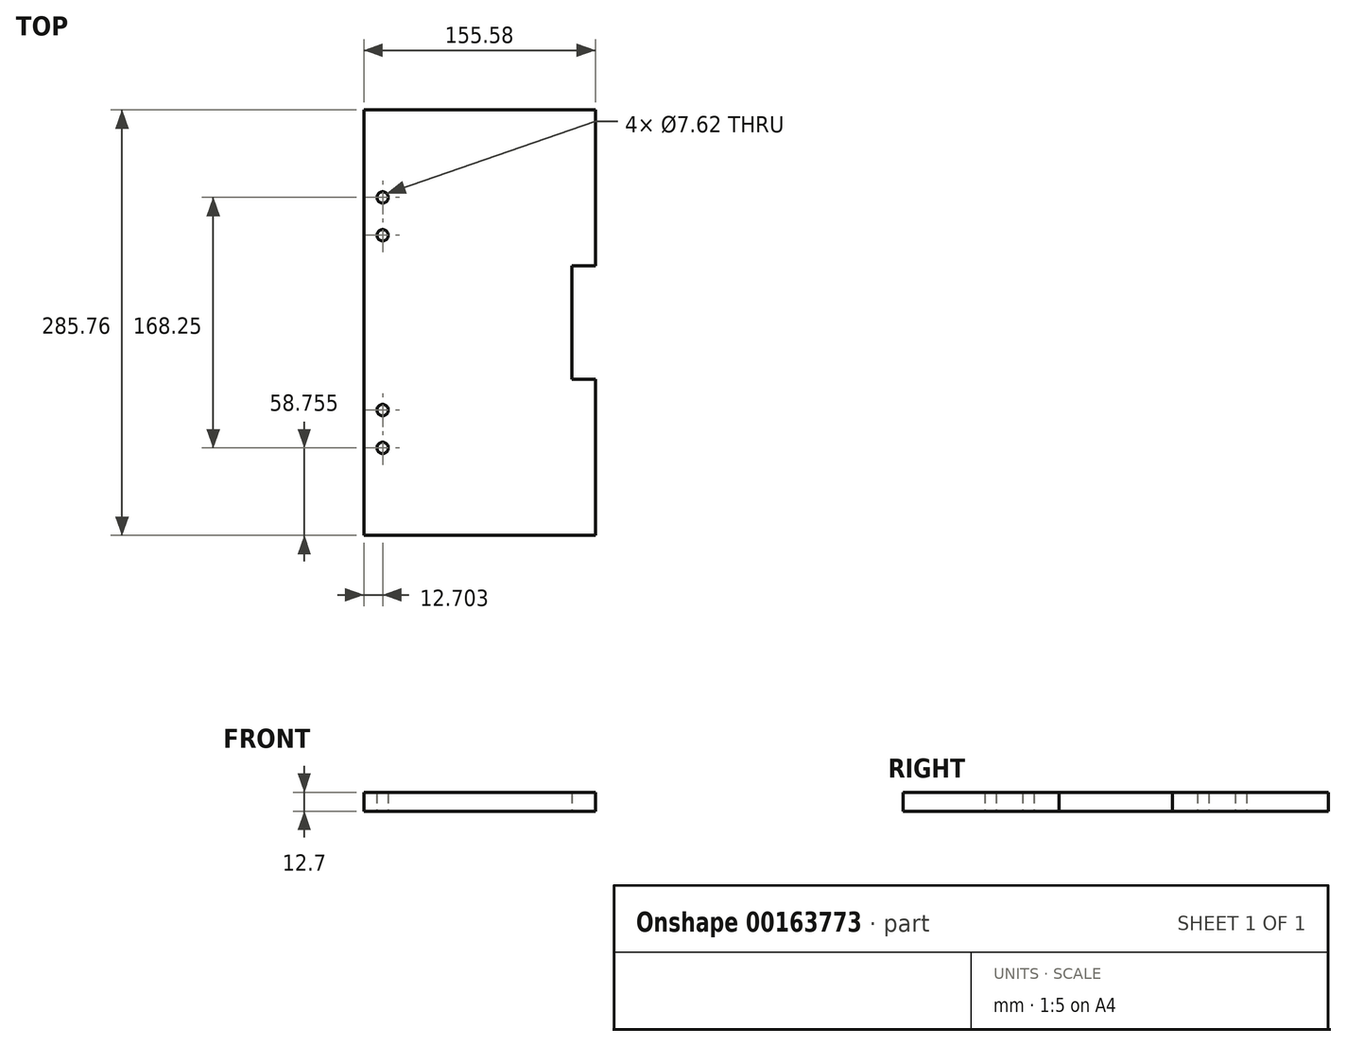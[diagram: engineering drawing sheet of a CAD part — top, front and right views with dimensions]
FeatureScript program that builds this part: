
annotation { "Feature Type Name" : "Feature", "Feature Type Description" : "" }
export const myFeature = defineFeature(function(context is Context, id is Id, definition is map)
    precondition{}
    {
        {
            var Q0;
            Q0=qCreatedBy(makeId("Top.planeOp"),FACE);
            var sketch = newSketch(context, id + "F0", { "sketchPlane" : qUnion([Q0])});
            skLineSegment(sketch, "E0.bottom", {"start": v(77.79, 142.88) * mm, "end": v(-77.79, 142.88) * mm});
            skLineSegment(sketch, "E0.top", {"start": v(77.79, -142.88) * mm, "end": v(-77.79, -142.88) * mm});
            skLineSegment(sketch, "E0.left", {"start": v(77.79, 142.88) * mm, "end": v(77.79, 38.1) * mm});
            skLineSegment(sketch, "E0.right", {"start": v(-77.79, 142.88) * mm, "end": v(-77.79, -142.88) * mm});
            skPoint(sketch, "E0.middle", {"position": v(0, 0) * mm});
            skLineSegment(sketch, "E1.bottom", {"start": v(77.79, -38.1) * mm, "end": v(61.91, -38.1) * mm});
            skLineSegment(sketch, "E1.top", {"start": v(77.79, 38.1) * mm, "end": v(61.91, 38.1) * mm});
            skLineSegment(sketch, "E1.right", {"start": v(61.91, -38.1) * mm, "end": v(61.91, 38.1) * mm});
            skPoint(sketch, "E1.left.end.orphan", {"position": v(93.66, 38.1) * mm});
            skPoint(sketch, "E2.orphan", {"position": v(93.66, -38.1) * mm});
            skLineSegment(sketch, "E3.trimOffspring", {"start": v(77.79, -38.1) * mm, "end": v(77.79, -142.88) * mm});
            skLineSegment(sketch, "E4", {"start": v(-77.79, 0) * mm, "end": v(-77.79, 71.42) * mm});
            skLineSegment(sketch, "E5", {"start": v(-77.79, 0) * mm, "end": v(-77.79, -71.42) * mm});
            skLineSegment(sketch, "E6.bottom", {"start": v(-52.39, -46.02) * mm, "end": v(-77.79, -46.02) * mm, "construction": true});
            skLineSegment(sketch, "E6.top", {"start": v(-52.39, -96.82) * mm, "end": v(-77.79, -96.82) * mm, "construction": true});
            skLineSegment(sketch, "E6.left", {"start": v(-52.39, -46.02) * mm, "end": v(-52.39, -96.82) * mm, "construction": true});
            skPoint(sketch, "E6.middle", {"position": v(-77.79, -71.42) * mm});
            skLineSegment(sketch, "E7.bottom", {"start": v(-52.39, 96.82) * mm, "end": v(-77.79, 96.82) * mm, "construction": true});
            skLineSegment(sketch, "E7.top", {"start": v(-52.39, 46.02) * mm, "end": v(-77.79, 46.02) * mm, "construction": true});
            skLineSegment(sketch, "E7.left", {"start": v(-52.39, 96.82) * mm, "end": v(-52.39, 46.02) * mm, "construction": true});
            skPoint(sketch, "E7.middle", {"position": v(-77.79, 71.42) * mm});
            skPoint(sketch, "E8.orphan", {"position": v(-103.19, 96.82) * mm});
            skPoint(sketch, "E9.orphan", {"position": v(-103.19, 46.02) * mm});
            skPoint(sketch, "E10.orphan", {"position": v(-103.19, -46.02) * mm});
            skPoint(sketch, "E11.orphan", {"position": v(-103.19, -96.82) * mm});
            skPoint(sketch, "E12.oppositeSnap0", {"position": v(-65.09, -46.02) * mm});
            skLineSegment(sketch, "E13.bottom", {"start": v(-52.39, -96.82) * mm, "end": v(-65.09, -96.82) * mm});
            skCircle(sketch, "E14", {"center": v(-65.09, -84.12) * mm, "radius": 3.81 * mm});
            skCircle(sketch, "E15", {"center": v(-65.09, -58.72) * mm, "radius": 3.81 * mm});
            skCircle(sketch, "E16", {"center": v(-65.09, 58.72) * mm, "radius": 3.81 * mm});
            skCircle(sketch, "E17", {"center": v(-65.09, 84.12) * mm, "radius": 3.81 * mm});
            skSolve(sketch);
        }
        {
            var Q0;
            {var subQ4=sQuery(id+"F0.wireOp",EDGE,"E0.bottom");Q0=makeQuery(id+"F0.imprint","IMPRINT",FACE,{"disambiguationData":[TD([[makeQuery(id+"F0.imprint","IMPRINT",EDGE,{"derivedFrom":subQ4}),1.0]])]});}
            extrude(context, id + "F1", {"entities" : qUnion([Q0]), "depth" : 12.7 * mm, "offsetDistance" : 25.4 * mm});
        }
    });
